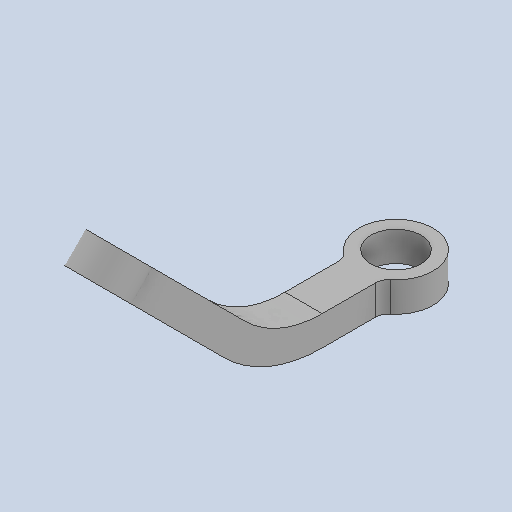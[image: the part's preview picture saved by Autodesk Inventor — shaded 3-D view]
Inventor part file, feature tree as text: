
AUTODESK INVENTOR PART (.ipt)
format: ipt  version: 2024 (Build 280153000, 153)  size: 319,488 bytes
history: native  units: mm
features: sketch x7, extrude x5, other x4, sweep x1, plane x1, mirror x1
ambient origin geometry x8: Origin, YZ Plane, XZ Plane, XY Plane, X Axis, Y Axis, Z Axis, Center Point
bodies: Solid1 (feature_tree)
feature tree (19):
  extrude  "Extrusion1"  Depth=12.0mm TaperAngle=0.0deg
  sweep  "Sweep2"
  plane  "Work Plane11"
  extrude  "Extrusion17"  TaperAngle=135.0deg  [1 undecoded]
  extrude  "Extrusion18"  TaperAngle=0.0deg  [1 undecoded]
  other  "Work Axis1"
  other  "Work Point1"
  extrude  "Extrusion19"  Depth=12.0mm TaperAngle=0.0deg
  other  "Work Point2"
  extrude  "Extrusion20"  Depth=15.0mm
  mirror  "Mirror2"
  sketch  "Sketch1"  dims[d0=30.0mm d1=12.0mm d2=0.0mm]
  sketch  "Sketch22"  dims[d109=5.0mm d110=35.0mm]
  sketch  "Sketch23"  dims[d111=70.0mm d112=135.0deg]
  sketch  "Sketch24"  dims[d113=50.0mm d114=0.0mm d115=0.0mm]
  sketch  "Sketch25"  dims[d116=-6.0mm d121=12.0mm d122=0.0mm]
  other  "Work Axis2"
  sketch  "Sketch26"  dims[d124=0.0mm d125=0.0mm d129=15.0mm]
  sketch  "Sketch27"  dims[d131=10.0mm d132=12.990381mm d133=20.2mm d134=10.0mm d135=0.0mm d136=22.0mm d137=12.0mm d138=5.0mm d139=16.2mm d140=5.0mm d141=0.0mm d74=0.5mm d75=0.872665mm d76=0.5mm d77=0.872665mm d98=0.0mm d99=0.0mm d100=0.0mm d101=0.0mm d102=0.872665mm d103=0.5mm d104=0.872665mm]
note: 2 required parameter values undecoded (feature->parameter linkage not recoverable at this tier; creation-order binding heuristic only, values carry confidence <= 0.55)
